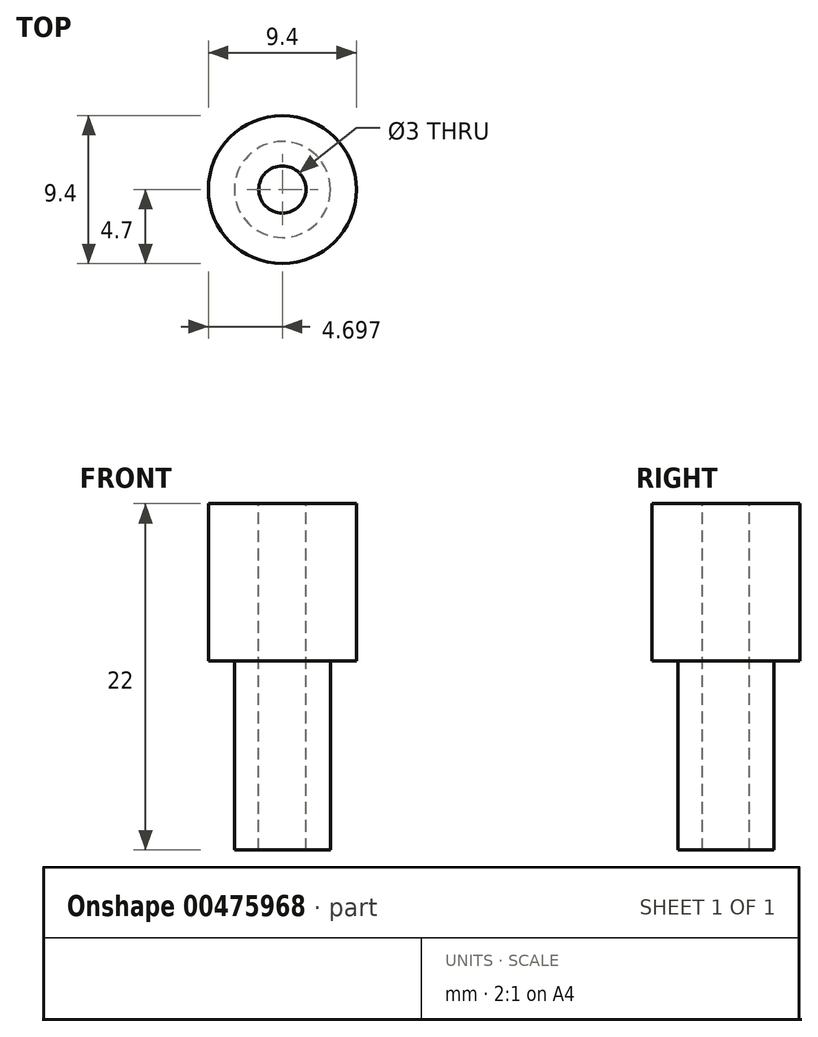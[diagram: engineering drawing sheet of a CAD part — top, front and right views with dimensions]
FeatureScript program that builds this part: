
annotation { "Feature Type Name" : "Feature", "Feature Type Description" : "" }
export const myFeature = defineFeature(function(context is Context, id is Id, definition is map)
    precondition{}
    {
        {
            var Q0;
            Q0=qCreatedBy(makeId("Front.planeOp"),FACE);
            var sketch = newSketch(context, id + "F0", { "sketchPlane" : qUnion([Q0])});
            skLineSegment(sketch, "E0", {"start": v(-113.93, 40.34) * mm, "end": v(-115.48, 40.34) * mm});
            skLineSegment(sketch, "E1", {"start": v(-115.48, 40.34) * mm, "end": v(-115.48, 52.34) * mm});
            skLineSegment(sketch, "E2", {"start": v(-115.48, 52.34) * mm, "end": v(-117.13, 52.34) * mm});
            skLineSegment(sketch, "E3", {"start": v(-117.13, 52.34) * mm, "end": v(-117.13, 62.34) * mm});
            skLineSegment(sketch, "E4", {"start": v(-117.13, 62.34) * mm, "end": v(-113.93, 62.34) * mm});
            skLineSegment(sketch, "E5", {"start": v(-113.93, 62.34) * mm, "end": v(-113.93, 40.34) * mm});
            skLineSegment(sketch, "E6", {"start": v(-112.43, 62.34) * mm, "end": v(-112.43, 40.46) * mm, "construction": true});
            skSolve(sketch);
        }
        {
            var Q0;
            Q0=qSketchRegion(id+"F0",true);
            var Q1;
            Q1=sQuery(id+"F0.wireOp",EDGE,"E6");
            revolve(context, id + "F1", {"entities" : qUnion([Q0]), "axis" : qUnion([Q1]), "revolveType" : RevolveType.FULL});
        }
    });
